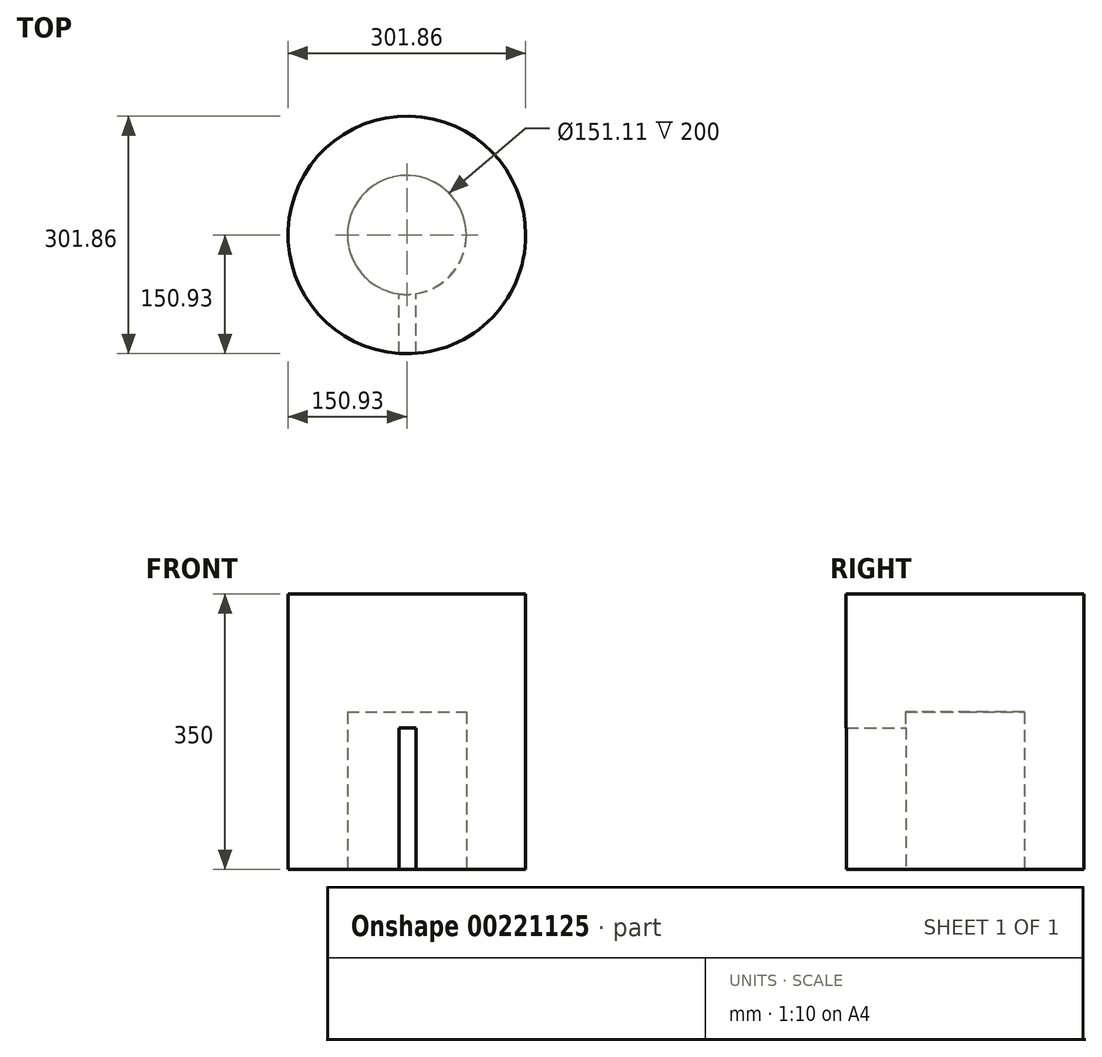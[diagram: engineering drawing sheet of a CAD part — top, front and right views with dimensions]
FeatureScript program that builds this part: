
annotation { "Feature Type Name" : "Feature", "Feature Type Description" : "" }
export const myFeature = defineFeature(function(context is Context, id is Id, definition is map)
    precondition{}
    {
        {
            var Q0;
            Q0=qCreatedBy(makeId("Top.planeOp"),FACE);
            var sketch = newSketch(context, id + "F0", { "sketchPlane" : qUnion([Q0])});
            skCircle(sketch, "E0", {"center": v(0, 0) * mm, "radius": 150.93 * mm});
            skSolve(sketch);
        }
        {
            var Q0;
            Q0=makeQuery(id+"F0.imprint","IMPRINT",FACE,{"disambiguationData":[TD([[makeQuery(id+"F0.imprint","IMPRINT",EDGE,{"derivedFrom":sQuery(id+"F0.wireOp",EDGE,"E0")}),1.0]])]});
            extrude(context, id + "F1", {"entities" : qUnion([Q0]), "depth" : 350 * mm});
        }
        {
            var Q0;
            Q0=makeQuery(id+"F1.opExtrude","CAP_FACE",FACE,{"disambiguationData":[OSD([sQuery(id+"F0.wireOp",EDGE,"E0")])],"isStart":true});
            var sketch = newSketch(context, id + "F2", { "sketchPlane" : qUnion([Q0])});
            skCircle(sketch, "E1", {"center": v(0, 0) * mm, "radius": 75.55 * mm});
            skSolve(sketch);
        }
        {
            var Q0;
            Q0=makeQuery(id+"F2.imprint","IMPRINT",FACE,{"disambiguationData":[TD([[makeQuery(id+"F2.imprint","IMPRINT",EDGE,{"derivedFrom":sQuery(id+"F2.wireOp",EDGE,"E1")}),1.0]])]});
            extrude(context, id + "F3", {"entities" : qUnion([Q0]), "operationType" : NewBodyOperationType.REMOVE, "oppositeDirection" : true, "depth" : 200 * mm});
        }
        {
            var Q0;
            Q0=makeQuery(id+"F1.opExtrude","CAP_FACE",FACE,{"disambiguationData":[OSD([sQuery(id+"F0.wireOp",EDGE,"E0")])],"isStart":true});
            var sketch = newSketch(context, id + "F4", { "sketchPlane" : qUnion([Q0])});
            skLineSegment(sketch, "E2", {"start": v(0, 0) * mm, "end": v(0, 195.4) * mm, "construction": true});
            skLineSegment(sketch, "E3.bottom", {"start": v(-9.75, 178.34) * mm, "end": v(11.38, 178.34) * mm});
            skLineSegment(sketch, "E3.top", {"start": v(-9.75, 58.9) * mm, "end": v(11.38, 58.9) * mm});
            skLineSegment(sketch, "E3.left", {"start": v(-9.75, 178.34) * mm, "end": v(-9.75, 58.9) * mm});
            skLineSegment(sketch, "E3.right", {"start": v(11.38, 178.34) * mm, "end": v(11.38, 58.9) * mm});
            skSolve(sketch);
        }
        {
            var Q0;
            Q0 = qSketchRegion(id + "F4", true);
            extrude(context, id + "F5", {"entities" : qUnion([Q0]), "operationType" : NewBodyOperationType.REMOVE, "oppositeDirection" : true, "depth" : 180 * mm});
        }
    });
